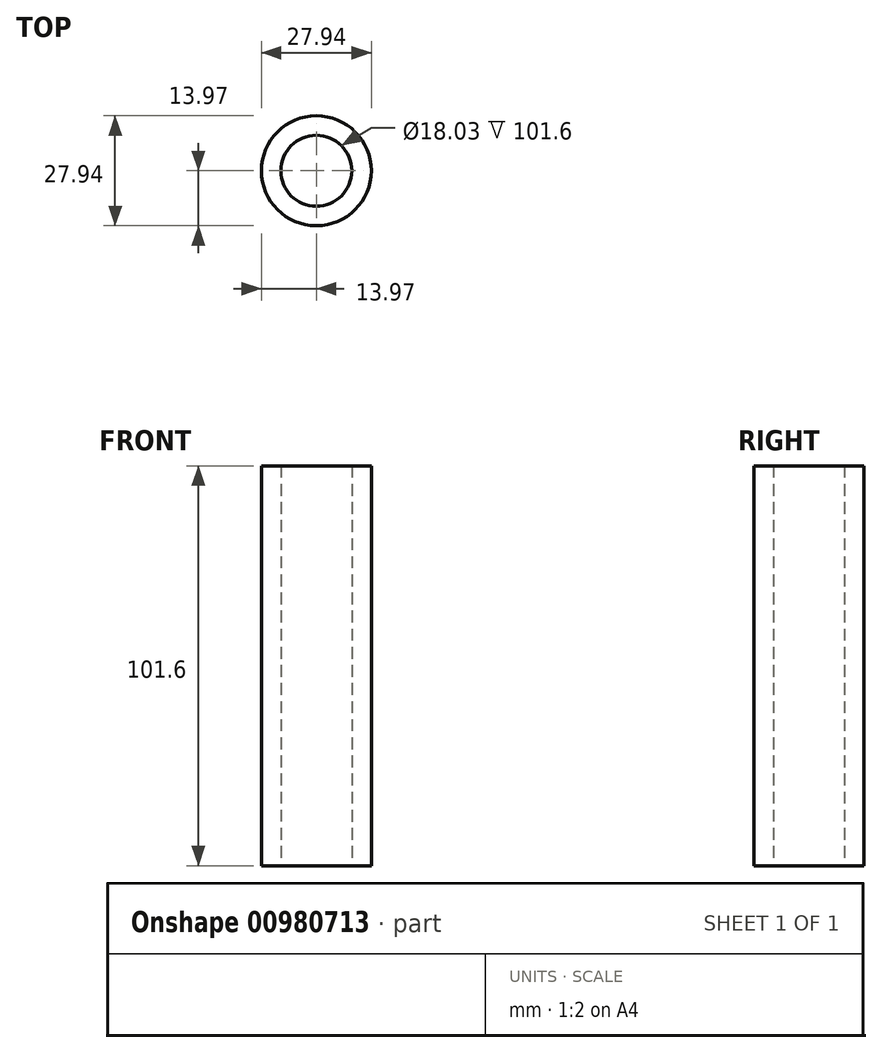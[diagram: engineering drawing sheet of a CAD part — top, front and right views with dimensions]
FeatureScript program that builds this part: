
annotation { "Feature Type Name" : "Feature", "Feature Type Description" : "" }
export const myFeature = defineFeature(function(context is Context, id is Id, definition is map)
    precondition{}
    {
        {
            var Q0;
            Q0=qCreatedBy(makeId("Top.planeOp"),FACE);
            var sketch = newSketch(context, id + "F0", { "sketchPlane" : qUnion([Q0])});
            skCircle(sketch, "E0", {"center": v(0, 0) * mm, "radius": 9.02 * mm});
            skCircle(sketch, "E1", {"center": v(0, 0) * mm, "radius": 13.97 * mm});
            skSolve(sketch);
        }
        {
            var Q0;
            Q0=makeQuery(id+"F0.imprint","IMPRINT",FACE,{"disambiguationData":[TD([[makeQuery(id+"F0.imprint","IMPRINT",EDGE,{"derivedFrom":sQuery(id+"F0.wireOp",EDGE,"E0")}),-1.0]])]});
            extrude(context, id + "F1", {"entities" : qUnion([Q0]), "depth" : 101.6 * mm, "offsetDistance" : 25.4 * mm});
        }
    });
